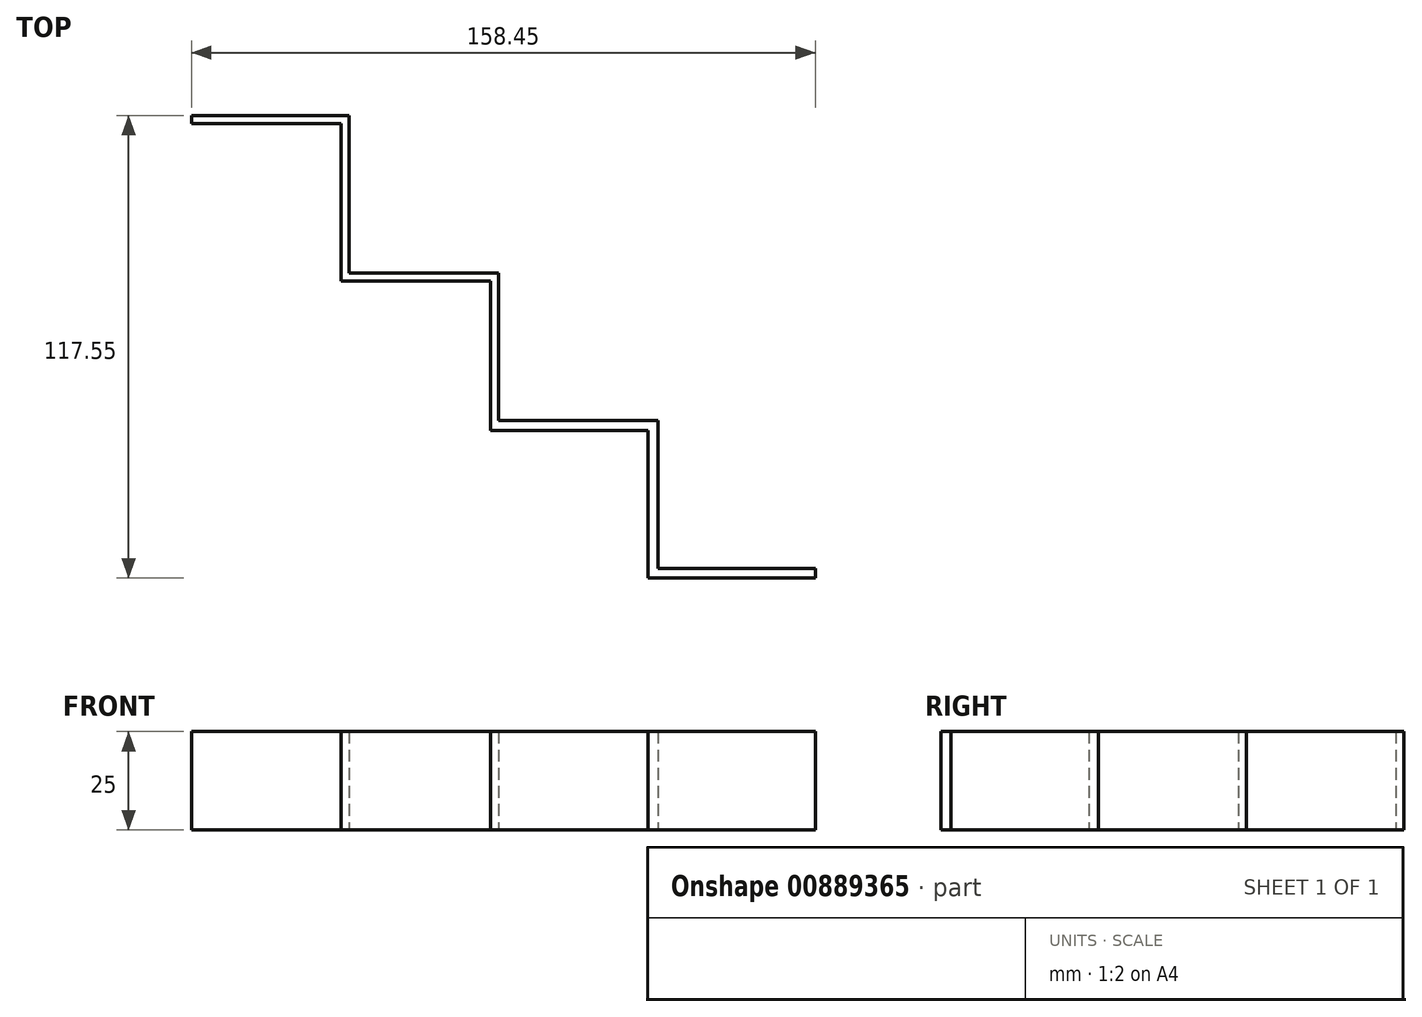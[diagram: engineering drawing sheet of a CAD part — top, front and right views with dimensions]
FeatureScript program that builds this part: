
annotation { "Feature Type Name" : "Feature", "Feature Type Description" : "" }
export const myFeature = defineFeature(function(context is Context, id is Id, definition is map)
    precondition{}
    {
        {
            var Q0;
            Q0=qCreatedBy(makeId("Top.planeOp"),FACE);
            var sketch = newSketch(context, id + "F0", { "sketchPlane" : qUnion([Q0])});
            skLineSegment(sketch, "E0.bottom", {"start": v(-24.79, -31.05) * mm, "end": v(15.21, -31.05) * mm});
            skLineSegment(sketch, "E0.top", {"start": v(-24.79, -29.05) * mm, "end": v(15.21, -29.05) * mm});
            skLineSegment(sketch, "E0.left", {"start": v(-24.79, -29.05) * mm, "end": v(-24.79, -31.05) * mm});
            skLineSegment(sketch, "E0.right", {"start": v(15.21, -29.05) * mm, "end": v(15.21, -31.05) * mm});
            skLineSegment(sketch, "E1.bottom", {"start": v(15.21, -31.05) * mm, "end": v(13.21, -31.05) * mm});
            skLineSegment(sketch, "E1.top", {"start": v(15.21, -71.05) * mm, "end": v(13.21, -71.05) * mm});
            skLineSegment(sketch, "E1.left", {"start": v(15.21, -31.05) * mm, "end": v(15.21, -71.05) * mm});
            skLineSegment(sketch, "E1.right", {"start": v(13.21, -31.05) * mm, "end": v(13.21, -71.05) * mm});
            skLineSegment(sketch, "E2.bottom", {"start": v(13.21, -71.05) * mm, "end": v(53.21, -71.05) * mm});
            skLineSegment(sketch, "E2.top", {"start": v(13.21, -69.05) * mm, "end": v(53.21, -69.05) * mm});
            skLineSegment(sketch, "E2.left", {"start": v(13.21, -71.05) * mm, "end": v(13.21, -69.05) * mm});
            skLineSegment(sketch, "E2.right", {"start": v(53.21, -71.05) * mm, "end": v(53.21, -69.05) * mm});
            skLineSegment(sketch, "E3.bottom", {"start": v(53.21, -69.05) * mm, "end": v(51.21, -69.05) * mm});
            skLineSegment(sketch, "E3.top", {"start": v(53.21, -109.05) * mm, "end": v(51.21, -109.05) * mm});
            skLineSegment(sketch, "E3.left", {"start": v(53.21, -69.05) * mm, "end": v(53.21, -109.05) * mm});
            skLineSegment(sketch, "E3.right", {"start": v(51.21, -69.05) * mm, "end": v(51.21, -109.05) * mm});
            skLineSegment(sketch, "E4.bottom", {"start": v(51.21, -109.05) * mm, "end": v(91.21, -109.05) * mm});
            skLineSegment(sketch, "E4.top", {"start": v(51.21, -106.6) * mm, "end": v(91.21, -106.6) * mm});
            skLineSegment(sketch, "E4.left", {"start": v(51.21, -109.05) * mm, "end": v(51.21, -106.6) * mm});
            skLineSegment(sketch, "E4.right", {"start": v(91.21, -109.05) * mm, "end": v(91.21, -106.6) * mm});
            skLineSegment(sketch, "E5.bottom", {"start": v(93.66, -106.6) * mm, "end": v(91.21, -106.6) * mm});
            skLineSegment(sketch, "E5.top", {"start": v(93.66, -146.6) * mm, "end": v(91.21, -146.6) * mm});
            skLineSegment(sketch, "E5.left", {"start": v(91.21, -106.6) * mm, "end": v(91.21, -146.6) * mm});
            skLineSegment(sketch, "E5.right", {"start": v(93.66, -106.6) * mm, "end": v(93.66, -146.6) * mm});
            skLineSegment(sketch, "E6.bottom", {"start": v(93.66, -146.6) * mm, "end": v(133.66, -146.6) * mm});
            skLineSegment(sketch, "E6.top", {"start": v(93.66, -144.15) * mm, "end": v(133.66, -144.15) * mm});
            skLineSegment(sketch, "E6.left", {"start": v(93.66, -146.6) * mm, "end": v(93.66, -144.15) * mm});
            skLineSegment(sketch, "E6.right", {"start": v(133.66, -146.6) * mm, "end": v(133.66, -144.15) * mm});
            skSolve(sketch);
        }
        {
            var Q0;
            Q0 = qSketchRegion(id + "F0", true);
            extrude(context, id + "F1", {"entities" : qUnion([Q0]), "depth" : 25 * mm, "offsetDistance" : 25 * mm});
        }
    });
